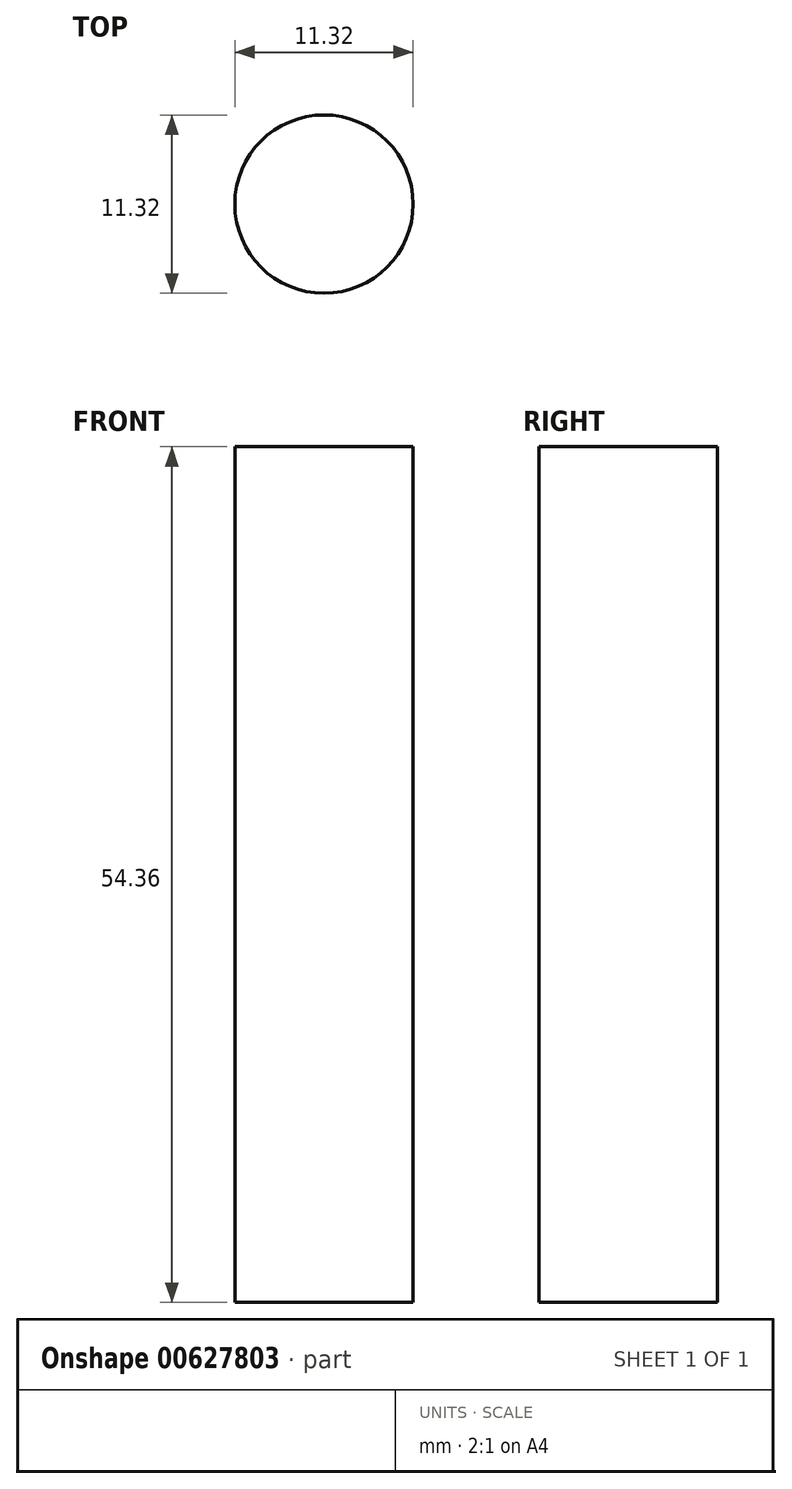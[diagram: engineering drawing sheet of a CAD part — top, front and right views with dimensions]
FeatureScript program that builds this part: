
annotation { "Feature Type Name" : "Feature", "Feature Type Description" : "" }
export const myFeature = defineFeature(function(context is Context, id is Id, definition is map)
    precondition{}
    {
        {
            var Q0;
            Q0=qCreatedBy(makeId("Top.planeOp"),FACE);
            var sketch = newSketch(context, id + "F0", { "sketchPlane" : qUnion([Q0])});
            skCircle(sketch, "E0", {"center": v(0, 0) * mm, "radius": 5.66 * mm});
            skSolve(sketch);
        }
        {
            var Q0;
            Q0=makeQuery(id+"F0.imprint","IMPRINT",FACE,{"disambiguationData":[TD([[makeQuery(id+"F0.imprint","IMPRINT",EDGE,{"derivedFrom":sQuery(id+"F0.wireOp",EDGE,"E0")}),1.0]])]});
            extrude(context, id + "F1", {"entities" : qUnion([Q0]), "depth" : 54.36 * mm, "offsetDistance" : 25.4 * mm});
        }
    });
